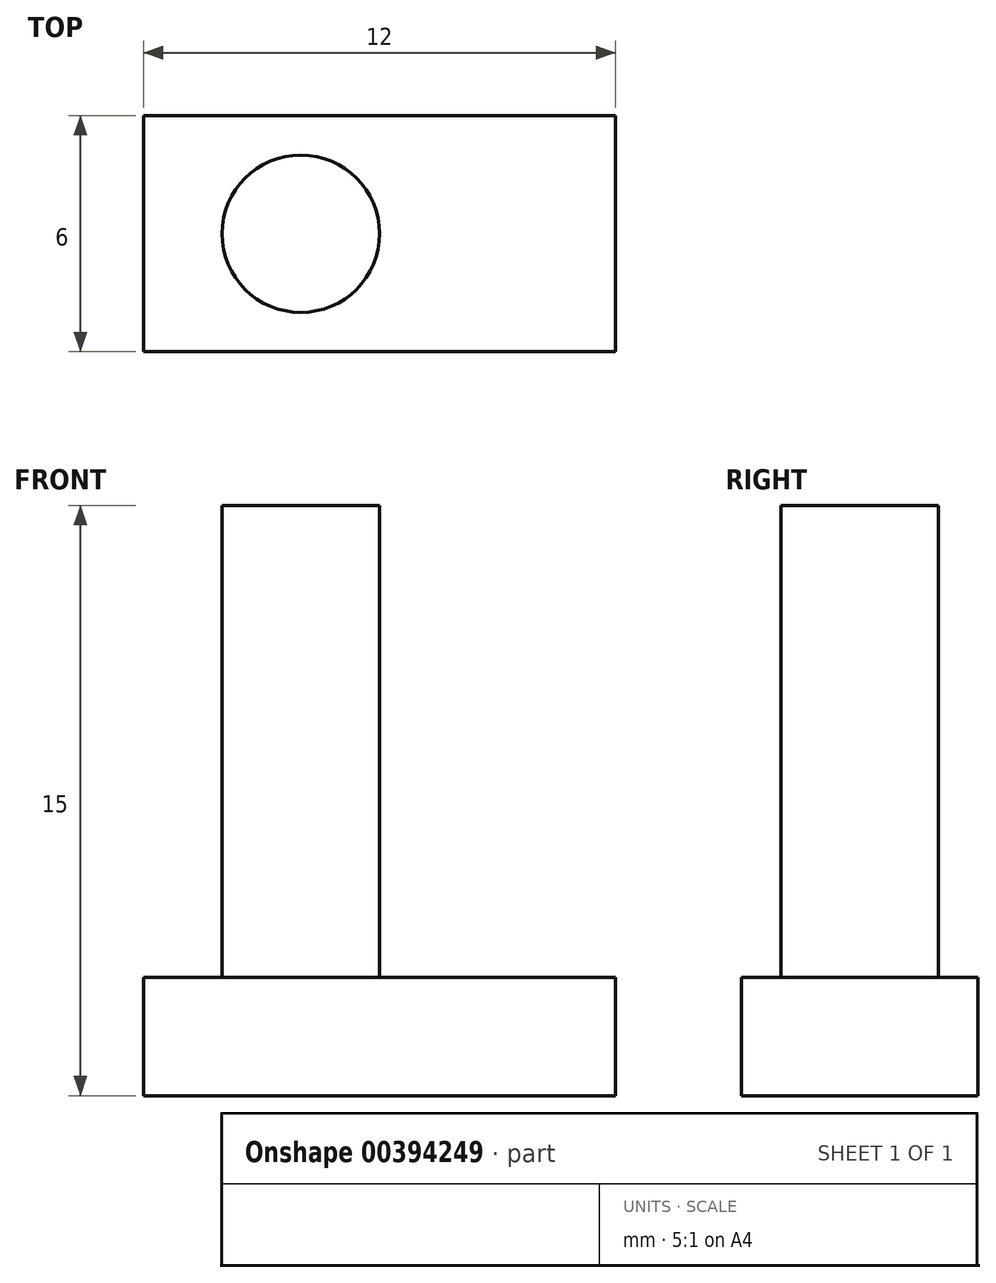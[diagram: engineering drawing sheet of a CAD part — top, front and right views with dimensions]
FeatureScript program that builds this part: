
annotation { "Feature Type Name" : "Feature", "Feature Type Description" : "" }
export const myFeature = defineFeature(function(context is Context, id is Id, definition is map)
    precondition{}
    {
        {
            var Q0;
            Q0=qCreatedBy(makeId("Top.planeOp"),FACE);
            var sketch = newSketch(context, id + "F0", { "sketchPlane" : qUnion([Q0])});
            skCircle(sketch, "E0", {"center": v(0, 0) * mm, "radius": 2 * mm});
            skSolve(sketch);
        }
        {
            var Q0;
            Q0 = qSketchRegion(id + "F0", true);
            extrude(context, id + "F1", {"entities" : qUnion([Q0]), "endBound" : BoundingType.SYMMETRIC, "depth" : 12 * mm});
        }
        {
            var Q0;
            Q0=makeQuery(id+"F1.opExtrude","CAP_FACE",FACE,{"disambiguationData":[OSD([sQuery(id+"F0.wireOp",EDGE,"E0")])],"isStart":true});
            var sketch = newSketch(context, id + "F2", { "sketchPlane" : qUnion([Q0])});
            skLineSegment(sketch, "E1.bottom", {"start": v(-4, 3) * mm, "end": v(8, 3) * mm});
            skLineSegment(sketch, "E1.top", {"start": v(-4, -3) * mm, "end": v(8, -3) * mm});
            skLineSegment(sketch, "E1.left", {"start": v(-4, 3) * mm, "end": v(-4, -3) * mm});
            skLineSegment(sketch, "E1.right", {"start": v(8, 3) * mm, "end": v(8, -3) * mm});
            skLineSegment(sketch, "E2", {"start": v(-4, 0) * mm, "end": v(8, 0) * mm, "construction": true});
            skCircle(sketch, "E3.0", {"center": v(0, 0) * mm, "radius": 2 * mm, "construction": true});
            skSolve(sketch);
        }
        {
            var Q0;
            Q0 = qSketchRegion(id + "F2", true);
            extrude(context, id + "F3", {"entities" : qUnion([Q0]), "operationType" : NewBodyOperationType.ADD, "depth" : 3 * mm});
        }
    });
